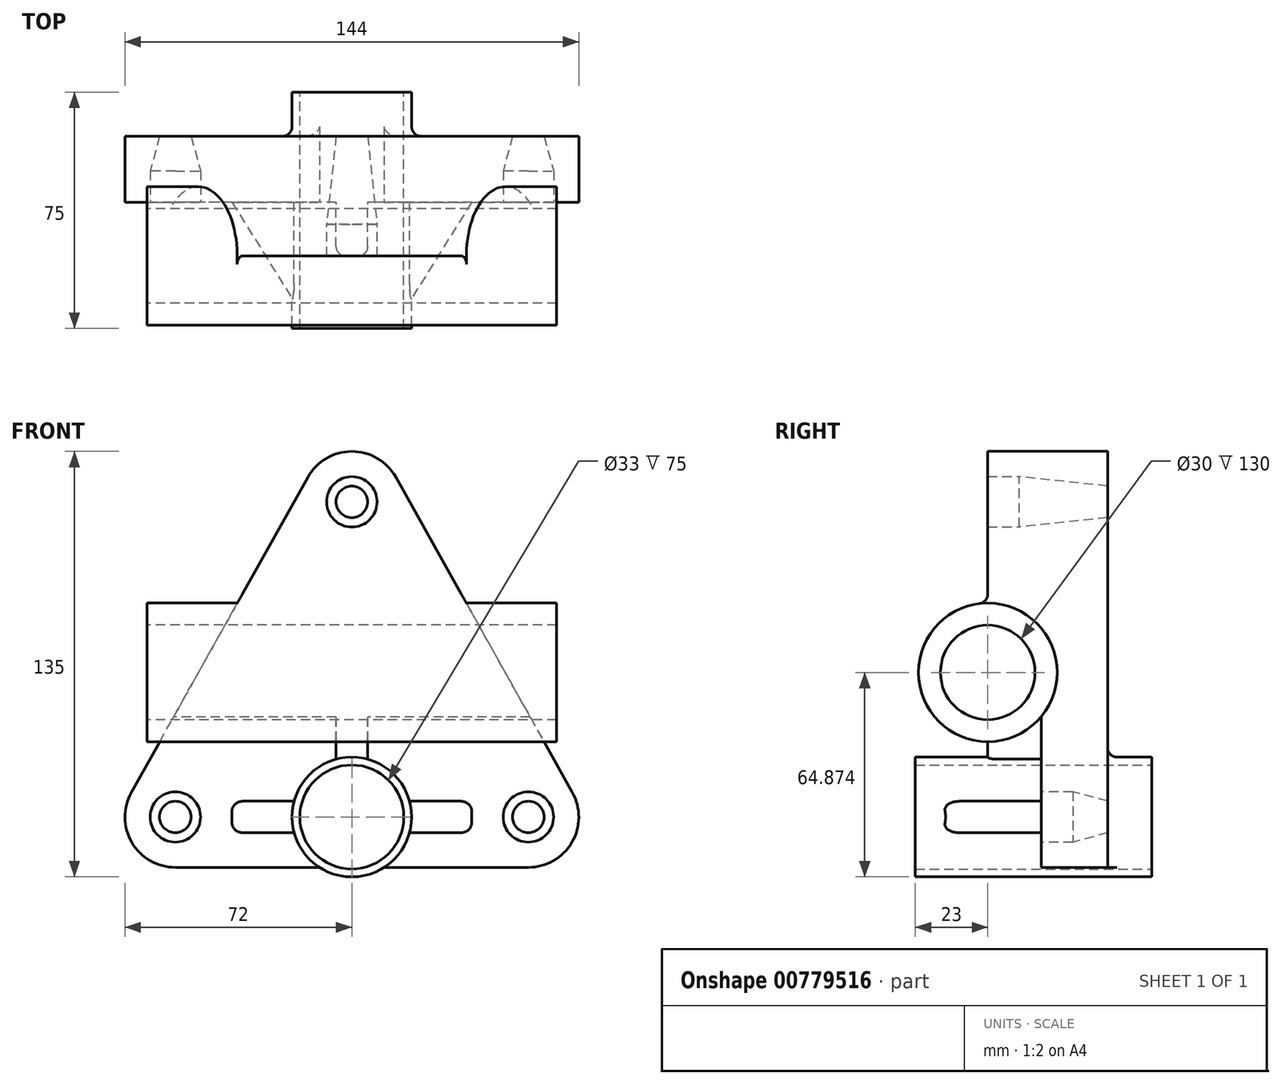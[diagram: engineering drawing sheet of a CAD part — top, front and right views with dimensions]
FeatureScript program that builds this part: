
annotation { "Feature Type Name" : "Feature", "Feature Type Description" : "" }
export const myFeature = defineFeature(function(context is Context, id is Id, definition is map)
    precondition{}
    {
        {
            var Q0;
            Q0=qCreatedBy(makeId("Front.planeOp"),FACE);
            var sketch = newSketch(context, id + "F0", { "sketchPlane" : qUnion([Q0])});
            skCircle(sketch, "E0", {"center": v(0, 0) * mm, "radius": 12.5 * mm});
            skCircle(sketch, "E1.0", {"center": v(0, 0) * mm, "radius": 19 * mm});
            skCircle(sketch, "E2.0", {"center": v(0, 0) * mm, "radius": 16.5 * mm});
            skCircle(sketch, "E3", {"center": v(-56, 0) * mm, "radius": 5 * mm});
            skCircle(sketch, "E4", {"center": v(-56, 0) * mm, "radius": 8 * mm});
            skCircle(sketch, "E5", {"center": v(56, 0) * mm, "radius": 8 * mm});
            skCircle(sketch, "E6", {"center": v(56, 0) * mm, "radius": 5 * mm});
            skCircle(sketch, "E7", {"center": v(0, 100) * mm, "radius": 5 * mm});
            skCircle(sketch, "E8", {"center": v(0, 100) * mm, "radius": 8 * mm});
            skArc(sketch, "E9.0", {"start": v(-69.96, 7.82) * mm, "mid": v(-69.8, -8.1) * mm, "end": v(-56, -16) * mm});
            skLineSegment(sketch, "E10", {"start": v(-10.25, -16) * mm, "end": v(-56, -16) * mm});
            skArc(sketch, "E11", {"start": v(13.96, 107.82) * mm, "mid": v(0, 116) * mm, "end": v(-13.96, 107.82) * mm});
            skLineSegment(sketch, "E12", {"start": v(-69.96, 7.82) * mm, "end": v(-13.96, 107.82) * mm});
            skLineSegment(sketch, "E13", {"start": v(10.25, -16) * mm, "end": v(56, -16) * mm});
            skArc(sketch, "E14.0", {"start": v(56, -16) * mm, "mid": v(69.8, -8.1) * mm, "end": v(69.96, 7.82) * mm});
            skLineSegment(sketch, "E15", {"start": v(13.96, 107.82) * mm, "end": v(69.96, 7.82) * mm});
            skLineSegment(sketch, "E16", {"start": v(0, 19) * mm, "end": v(0, -19) * mm, "construction": true});
            skLineSegment(sketch, "E17", {"start": v(-18.33, 5) * mm, "end": v(-38, 5) * mm});
            skLineSegment(sketch, "E18", {"start": v(-38, 5) * mm, "end": v(-38, -5) * mm});
            skLineSegment(sketch, "E19", {"start": v(-38, -5) * mm, "end": v(-18.33, -5) * mm});
            skLineSegment(sketch, "E20", {"start": v(18.33, 5) * mm, "end": v(38, 5) * mm});
            skLineSegment(sketch, "E21", {"start": v(38, 5) * mm, "end": v(38, -5) * mm});
            skLineSegment(sketch, "E22", {"start": v(38, -5) * mm, "end": v(18.33, -5) * mm});
            skLineSegment(sketch, "E23", {"start": v(-5, 31.73) * mm, "end": v(5, 31.73) * mm});
            skLineSegment(sketch, "E24", {"start": v(-5, 31.73) * mm, "end": v(-56.57, 31.73) * mm});
            skLineSegment(sketch, "E25", {"start": v(-56.57, 31.73) * mm, "end": v(56.57, 31.73) * mm});
            skLineSegment(sketch, "E26", {"start": v(-5, 31.73) * mm, "end": v(-5, 18.33) * mm});
            skLineSegment(sketch, "E27", {"start": v(5, 31.73) * mm, "end": v(5, 18.33) * mm});
            skSolve(sketch);
        }
        {
            var Q0;
            Q0=qCreatedBy(makeId("Right.planeOp"),FACE);
            var sketch = newSketch(context, id + "F1", { "sketchPlane" : qUnion([Q0])});
            skCircle(sketch, "E28", {"center": v(-17, 45.87) * mm, "radius": 22 * mm});
            skCircle(sketch, "E29", {"center": v(-17, 45.87) * mm, "radius": 15 * mm});
            skSolve(sketch);
        }
        {
            var Q0;
            Q0=makeQuery(id+"F0.imprint","IMPRINT",FACE,{"disambiguationData":[TD([[makeQuery(id+"F0.imprint","IMPRINT",EDGE,{"derivedFrom":sQuery(id+"F0.wireOp",EDGE,"E8")}),-1.0]])]});
            extrude(context, id + "F2", {"entities" : qUnion([Q0]), "depth" : 17 * mm, "offsetDistance" : 25 * mm});
        }
        {
            var Q0;
            Q0=makeQuery(id+"F0.imprint","IMPRINT",FACE,{"disambiguationData":[TD([[makeQuery(id+"F0.imprint","IMPRINT",EDGE,{"derivedFrom":sQuery(id+"F0.wireOp",EDGE,"E8")}),-1.0]])]});
            var Q1;
            Q1=makeQuery(id+"F0.imprint","IMPRINT",FACE,{"disambiguationData":[TD([[makeQuery(id+"F0.imprint","IMPRINT",EDGE,{"derivedFrom":sQuery(id+"F0.wireOp",EDGE,"E5")}),-1.0]])]});
            var Q2;
            Q2=makeQuery(id+"F0.imprint","IMPRINT",FACE,{"disambiguationData":[TD([[makeQuery(id+"F0.imprint","IMPRINT",EDGE,{"derivedFrom":sQuery(id+"F0.wireOp",EDGE,"E4")}),-1.0]])]});
            var Q3;
            {var subQ0=sQuery(id+"F0.wireOp",EDGE,"E20");Q3=makeQuery(id+"F0.imprint","IMPRINT",FACE,{"disambiguationData":[TD([[makeQuery(id+"F0.imprint","IMPRINT",EDGE,{"derivedFrom":subQ0}),-1.0]])]});}
            var Q4;
            {var subQ0=sQuery(id+"F0.wireOp",EDGE,"E17");Q4=makeQuery(id+"F0.imprint","IMPRINT",FACE,{"disambiguationData":[TD([[makeQuery(id+"F0.imprint","IMPRINT",EDGE,{"derivedFrom":subQ0}),1.0]])]});}
            extrude(context, id + "F3", {"entities" : qUnion([Q0, Q1, Q2, Q3, Q4]), "operationType" : NewBodyOperationType.ADD, "oppositeDirection" : true, "depth" : 21 * mm, "offsetDistance" : 25 * mm});
        }
        {
            var Q0;
            Q0=makeQuery(id+"F1.imprint","IMPRINT",FACE,{"disambiguationData":[TD([[makeQuery(id+"F1.imprint","IMPRINT",EDGE,{"derivedFrom":sQuery(id+"F1.wireOp",EDGE,"E28")}),1.0]])]});
            extrude(context, id + "F4", {"entities" : qUnion([Q0]), "operationType" : NewBodyOperationType.ADD, "endBound" : BoundingType.SYMMETRIC, "depth" : 130 * mm, "offsetDistance" : 25 * mm});
        }
        {
            var Q0;
            Q0=makeQuery(id+"F1.imprint","IMPRINT",FACE,{"disambiguationData":[TD([[makeQuery(id+"F1.imprint","IMPRINT",EDGE,{"derivedFrom":sQuery(id+"F1.wireOp",EDGE,"E29")}),1.0]])]});
            extrude(context, id + "F5", {"entities" : qUnion([Q0]), "operationType" : NewBodyOperationType.REMOVE, "endBound" : BoundingType.SYMMETRIC, "oppositeDirection" : true, "depth" : 130 * mm, "offsetDistance" : 25 * mm});
        }
        {
            var Q0;
            {var subQ0=sQuery(id+"F0.wireOp",EDGE,"E17");Q0=makeQuery(id+"F0.imprint","IMPRINT",FACE,{"disambiguationData":[TD([[makeQuery(id+"F0.imprint","IMPRINT",EDGE,{"derivedFrom":subQ0}),1.0]])]});}
            var Q1;
            {var subQ0=sQuery(id+"F0.wireOp",EDGE,"E20");Q1=makeQuery(id+"F0.imprint","IMPRINT",FACE,{"disambiguationData":[TD([[makeQuery(id+"F0.imprint","IMPRINT",EDGE,{"derivedFrom":subQ0}),-1.0]])]});}
            extrude(context, id + "F6", {"entities" : qUnion([Q0, Q1]), "operationType" : NewBodyOperationType.ADD, "depth" : 32 * mm, "offsetDistance" : 25 * mm});
        }
        {
            var Q0;
            Q0=makeQuery(id+"F0.imprint","IMPRINT",FACE,{"disambiguationData":[TD([[makeQuery(id+"F0.imprint","IMPRINT",EDGE,{"derivedFrom":sQuery(id+"F0.wireOp",EDGE,"E2.0")}),-1.0]])]});
            extrude(context, id + "F7", {"entities" : qUnion([Q0]), "depth" : 40 * mm, "offsetDistance" : 25 * mm});
        }
        {
            var Q0;
            Q0=makeQuery(id+"F0.imprint","IMPRINT",FACE,{"disambiguationData":[TD([[makeQuery(id+"F0.imprint","IMPRINT",EDGE,{"derivedFrom":sQuery(id+"F0.wireOp",EDGE,"E2.0")}),-1.0]])]});
            extrude(context, id + "F8", {"entities" : qUnion([Q0]), "oppositeDirection" : true, "depth" : 35 * mm, "offsetDistance" : 25 * mm});
        }
        {
            var Q0;
            Q0=makeQuery(id+"F6.opExtrude","CAP_EDGE",EDGE,{"disambiguationData":[OSD([sQuery(id+"F0.wireOp",EDGE,"E18")])],"isStart":false});
            chamfer(context, id + "F9", {"entities" : qUnion([Q0]), "chamferType" : ChamferType.TWO_OFFSETS, "width1" : 20 * mm, "oppositeDirection" : false, "width2" : 32 * mm, "tangentPropagation" : true});
        }
        {
            var Q0;
            Q0=makeQuery(id+"F6.opExtrude","CAP_EDGE",EDGE,{"disambiguationData":[OSD([sQuery(id+"F0.wireOp",EDGE,"E21")])],"isStart":false});
            chamfer(context, id + "F10", {"entities" : qUnion([Q0]), "chamferType" : ChamferType.TWO_OFFSETS, "width1" : 32 * mm, "oppositeDirection" : false, "width2" : 20 * mm, "tangentPropagation" : true});
        }
        {
            var Q0;
            {var subQ0=sQuery(id+"F0.wireOp",EDGE,"E26");Q0=makeQuery(id+"F0.imprint","IMPRINT",FACE,{"disambiguationData":[TD([[makeQuery(id+"F0.imprint","IMPRINT",EDGE,{"derivedFrom":subQ0}),1.0]])]});}
            extrude(context, id + "F11", {"entities" : qUnion([Q0]), "operationType" : NewBodyOperationType.ADD, "oppositeDirection" : true, "depth" : 21 * mm, "offsetDistance" : 25 * mm});
        }
        {
            var Q0;
            {var subQ0=sQuery(id+"F0.wireOp",EDGE,"E26");Q0=makeQuery(id+"F0.imprint","IMPRINT",FACE,{"disambiguationData":[TD([[makeQuery(id+"F0.imprint","IMPRINT",EDGE,{"derivedFrom":subQ0}),1.0]])]});}
            extrude(context, id + "F12", {"entities" : qUnion([Q0]), "operationType" : NewBodyOperationType.ADD, "depth" : 17 * mm, "offsetDistance" : 25 * mm});
        }
        {
            var Q0;
            Q0=makeQuery(id+"F1.imprint","IMPRINT",FACE,{"disambiguationData":[TD([[makeQuery(id+"F1.imprint","IMPRINT",EDGE,{"derivedFrom":sQuery(id+"F1.wireOp",EDGE,"E29")}),1.0]])]});
            extrude(context, id + "F13", {"entities" : qUnion([Q0]), "operationType" : NewBodyOperationType.REMOVE, "endBound" : BoundingType.SYMMETRIC, "oppositeDirection" : true, "depth" : 130 * mm, "offsetDistance" : 25 * mm});
        }
        {
            var Q0;
            {var subQ0=sQuery(id+"F0.wireOp",EDGE,"E27");var subQ1=sQuery(id+"F0.wireOp",EDGE,"E26");var subQ2=sQuery(id+"F0.wireOp",EDGE,"E25");var subQ3=sQuery(id+"F0.wireOp",EDGE,"E1.0");Q0=makeQuery(id+"F11.boolean.opBoolean","MERGE",FACE,{"derivedFrom":[makeQuery(id+"F3.opExtrude","CAP_FACE",FACE,{"disambiguationData":[OSD([subQ3,sQuery(id+"F0.wireOp",EDGE,"E4"),sQuery(id+"F0.wireOp",EDGE,"E5"),sQuery(id+"F0.wireOp",EDGE,"E8"),sQuery(id+"F0.wireOp",EDGE,"E9.0"),sQuery(id+"F0.wireOp",EDGE,"E10"),sQuery(id+"F0.wireOp",EDGE,"E11"),sQuery(id+"F0.wireOp",EDGE,"E12"),sQuery(id+"F0.wireOp",EDGE,"E13"),sQuery(id+"F0.wireOp",EDGE,"E14.0"),sQuery(id+"F0.wireOp",EDGE,"E15"),subQ2,subQ1,subQ0])],"isStart":false}),makeQuery(id+"F11.opExtrude","CAP_FACE",FACE,{"disambiguationData":[OSD([subQ3,subQ2,subQ1,subQ0])],"isStart":false})]});}
            var sketch = newSketch(context, id + "F14", { "sketchPlane" : qUnion([Q0])});
            skCircle(sketch, "E30", {"center": v(-56, 0) * mm, "radius": 8 * mm});
            skCircle(sketch, "E31", {"center": v(56, 0) * mm, "radius": 8 * mm});
            skCircle(sketch, "E32", {"center": v(0, 100) * mm, "radius": 8 * mm});
            skCircle(sketch, "E33", {"center": v(0, 100) * mm, "radius": 5 * mm});
            skCircle(sketch, "E34", {"center": v(-56, 0) * mm, "radius": 5 * mm});
            skCircle(sketch, "E35", {"center": v(56, 0) * mm, "radius": 5 * mm});
            skSolve(sketch);
        }
        {
            var Q0;
            Q0=makeQuery(id+"F14.imprint","IMPRINT",FACE,{"disambiguationData":[TD([[makeQuery(id+"F14.imprint","IMPRINT",EDGE,{"derivedFrom":sQuery(id+"F14.wireOp",EDGE,"E30")}),-1.0]])]});
            var Q1;
            Q1=makeQuery(id+"F14.imprint","IMPRINT",FACE,{"disambiguationData":[TD([[makeQuery(id+"F14.imprint","IMPRINT",EDGE,{"derivedFrom":sQuery(id+"F14.wireOp",EDGE,"E31")}),-1.0]])]});
            extrude(context, id + "F15", {"entities" : qUnion([Q0, Q1]), "operationType" : NewBodyOperationType.ADD, "oppositeDirection" : true, "depth" : 11 * mm, "offsetDistance" : 25 * mm});
        }
        {
            var Q0;
            Q0=makeQuery(id+"F14.imprint","IMPRINT",FACE,{"disambiguationData":[TD([[makeQuery(id+"F14.imprint","IMPRINT",EDGE,{"derivedFrom":sQuery(id+"F14.wireOp",EDGE,"E32")}),-1.0]])]});
            extrude(context, id + "F16", {"entities" : qUnion([Q0]), "operationType" : NewBodyOperationType.ADD, "oppositeDirection" : true, "depth" : 28 * mm, "offsetDistance" : 25 * mm});
        }
        {
            var Q0;
            Q0=makeQuery(id+"F15.opExtrude","CAP_EDGE",EDGE,{"disambiguationData":[OSD([sQuery(id+"F14.wireOp",EDGE,"E35")])],"isStart":false});
            chamfer(context, id + "F17", {"entities" : qUnion([Q0]), "chamferType" : ChamferType.TWO_OFFSETS, "width1" : 3 * mm, "oppositeDirection" : false, "width2" : 11 * mm, "tangentPropagation" : true});
        }
        {
            var Q0;
            Q0=makeQuery(id+"F15.opExtrude","CAP_EDGE",EDGE,{"disambiguationData":[OSD([sQuery(id+"F14.wireOp",EDGE,"E34")])],"isStart":false});
            chamfer(context, id + "F18", {"entities" : qUnion([Q0]), "chamferType" : ChamferType.TWO_OFFSETS, "width1" : 3 * mm, "oppositeDirection" : false, "width2" : 11 * mm, "tangentPropagation" : true});
        }
        {
            var Q0;
            Q0=makeQuery(id+"F16.opExtrude","CAP_EDGE",EDGE,{"disambiguationData":[OSD([sQuery(id+"F14.wireOp",EDGE,"E33")])],"isStart":false});
            chamfer(context, id + "F19", {"entities" : qUnion([Q0]), "chamferType" : ChamferType.TWO_OFFSETS, "width1" : 3 * mm, "oppositeDirection" : false, "width2" : 28 * mm, "tangentPropagation" : true});
        }
        {
            var Q0;
            Q0=makeQuery(id+"F10.opChamfer","BLEND_EDGE",EDGE,{"blendedFrom":[makeQuery(id+"F6.opExtrude","CAP_EDGE",EDGE,{"disambiguationData":[OSD([sQuery(id+"F0.wireOp",EDGE,"E21")])],"isStart":false}),makeQuery(id+"F6.opExtrude","SWEPT_FACE",FACE,{"disambiguationData":[OSD([sQuery(id+"F0.wireOp",EDGE,"E20")])]})],"blendedInto":[makeQuery(id+"F6.opExtrude","SWEPT_FACE",FACE,{"disambiguationData":[OSD([sQuery(id+"F0.wireOp",EDGE,"E20")])]})]});
            var Q1;
            Q1=makeQuery(id+"F10.opChamfer","BLEND_EDGE",EDGE,{"blendedFrom":[makeQuery(id+"F6.opExtrude","CAP_EDGE",EDGE,{"disambiguationData":[OSD([sQuery(id+"F0.wireOp",EDGE,"E21")])],"isStart":false}),makeQuery(id+"F6.opExtrude","SWEPT_FACE",FACE,{"disambiguationData":[OSD([sQuery(id+"F0.wireOp",EDGE,"E22")])]})],"blendedInto":[makeQuery(id+"F6.opExtrude","SWEPT_FACE",FACE,{"disambiguationData":[OSD([sQuery(id+"F0.wireOp",EDGE,"E22")])]})]});
            var Q2;
            Q2=makeQuery(id+"F9.opChamfer","BLEND_EDGE",EDGE,{"blendedFrom":[makeQuery(id+"F6.opExtrude","CAP_EDGE",EDGE,{"disambiguationData":[OSD([sQuery(id+"F0.wireOp",EDGE,"E18")])],"isStart":false}),makeQuery(id+"F6.opExtrude","SWEPT_FACE",FACE,{"disambiguationData":[OSD([sQuery(id+"F0.wireOp",EDGE,"E19")])]})],"blendedInto":[makeQuery(id+"F6.opExtrude","SWEPT_FACE",FACE,{"disambiguationData":[OSD([sQuery(id+"F0.wireOp",EDGE,"E19")])]})]});
            var Q3;
            Q3=makeQuery(id+"F9.opChamfer","BLEND_EDGE",EDGE,{"blendedFrom":[makeQuery(id+"F6.opExtrude","CAP_EDGE",EDGE,{"disambiguationData":[OSD([sQuery(id+"F0.wireOp",EDGE,"E18")])],"isStart":false}),makeQuery(id+"F6.opExtrude","SWEPT_FACE",FACE,{"disambiguationData":[OSD([sQuery(id+"F0.wireOp",EDGE,"E17")])]})],"blendedInto":[makeQuery(id+"F6.opExtrude","SWEPT_FACE",FACE,{"disambiguationData":[OSD([sQuery(id+"F0.wireOp",EDGE,"E17")])]})]});
            var Q4;
            {var subQ0=sQuery(id+"F0.wireOp",EDGE,"E26");Q4=makeQuery(id+"F12.boolean.opBoolean","SPLIT",EDGE,{"disambiguationData":[TD([makeQuery(id+"F4.opExtrude","SWEPT_FACE",FACE,{"disambiguationData":[OSD([sQuery(id+"F1.wireOp",EDGE,"E28")])]})])],"derivedFrom":makeQuery(id+"F12.opExtrude","CAP_EDGE",EDGE,{"disambiguationData":[OSD([subQ0])],"isStart":false})});}
            var Q5;
            {var subQ0=sQuery(id+"F0.wireOp",EDGE,"E27");Q5=makeQuery(id+"F12.boolean.opBoolean","SPLIT",EDGE,{"disambiguationData":[TD([makeQuery(id+"F4.opExtrude","SWEPT_FACE",FACE,{"disambiguationData":[OSD([sQuery(id+"F1.wireOp",EDGE,"E28")])]})])],"derivedFrom":makeQuery(id+"F12.opExtrude","CAP_EDGE",EDGE,{"disambiguationData":[OSD([subQ0])],"isStart":false})});}
            var Q6;
            Q6=makeQuery(id+"F4.boolean.opBoolean","INTERSECT",EDGE,{"derivedFrom":[makeQuery(id+"F2.opExtrude","CAP_FACE",FACE,{"disambiguationData":[OSD([sQuery(id+"F0.wireOp",EDGE,"E8"),sQuery(id+"F0.wireOp",EDGE,"E11"),sQuery(id+"F0.wireOp",EDGE,"E12"),sQuery(id+"F0.wireOp",EDGE,"E15"),sQuery(id+"F0.wireOp",EDGE,"E25")])],"isStart":false}),makeQuery(id+"F4.opExtrude","SWEPT_FACE",FACE,{"disambiguationData":[OSD([sQuery(id+"F1.wireOp",EDGE,"E28")])]})]});
            var Q7;
            {var subQ0=sQuery(id+"F0.wireOp",EDGE,"E25");var subQ1=makeQuery(id+"F3.opExtrude","SWEPT_FACE",FACE,{"disambiguationData":[OSD([subQ0])]});var subQ2=sQuery(id+"F0.wireOp",EDGE,"E12");var subQ3=makeQuery(id+"F2.opExtrude","SWEPT_FACE",FACE,{"disambiguationData":[OSD([subQ0])]});var subQ4=makeQuery(id+"F4.opExtrude","SWEPT_FACE",FACE,{"disambiguationData":[OSD([sQuery(id+"F1.wireOp",EDGE,"E28")])]});Q7=makeQuery(id+"F12.boolean.opBoolean","SPLIT",EDGE,{"disambiguationData":[TD([makeQuery(id+"F2.opExtrude","SWEPT_FACE",FACE,{"disambiguationData":[OSD([subQ2])]})])],"derivedFrom":makeQuery(id+"F4.boolean.opBoolean","INTERSECT",EDGE,{"derivedFrom":[makeQuery(id+"F3.boolean.opBoolean","MERGE",FACE,{"derivedFrom":[subQ3,subQ1]}),subQ4]})});}
            var Q8;
            {var subQ0=sQuery(id+"F0.wireOp",EDGE,"E15");var subQ1=sQuery(id+"F0.wireOp",EDGE,"E25");var subQ2=makeQuery(id+"F2.opExtrude","SWEPT_FACE",FACE,{"disambiguationData":[OSD([subQ1])]});var subQ3=makeQuery(id+"F3.opExtrude","SWEPT_FACE",FACE,{"disambiguationData":[OSD([subQ1])]});var subQ4=makeQuery(id+"F4.opExtrude","SWEPT_FACE",FACE,{"disambiguationData":[OSD([sQuery(id+"F1.wireOp",EDGE,"E28")])]});Q8=makeQuery(id+"F12.boolean.opBoolean","SPLIT",EDGE,{"disambiguationData":[TD([makeQuery(id+"F2.opExtrude","SWEPT_FACE",FACE,{"disambiguationData":[OSD([subQ0])]})])],"derivedFrom":makeQuery(id+"F4.boolean.opBoolean","INTERSECT",EDGE,{"derivedFrom":[makeQuery(id+"F3.boolean.opBoolean","MERGE",FACE,{"derivedFrom":[subQ2,subQ3]}),subQ4]})});}
            var Q9;
            Q9=makeQuery(id+"F12.opExtrude","CAP_EDGE",EDGE,{"disambiguationData":[OSD([sQuery(id+"F0.wireOp",EDGE,"E1.0")])],"isStart":false});
            var Q10;
            {var subQ0=sQuery(id+"F0.wireOp",EDGE,"E1.0");var subQ2=makeQuery(id+"F0.imprint","INTERSECT",VERTEX,{"derivedFrom":[subQ0,sQuery(id+"F0.wireOp",EDGE,"E17")]});var subQ3=makeQuery(id+"F0.imprint","INTERSECT",VERTEX,{"derivedFrom":[subQ0,sQuery(id+"F0.wireOp",EDGE,"E20")]});Q10=makeQuery(id+"F11.boolean.opBoolean","MERGE",EDGE,{"derivedFrom":[makeQuery(id+"F3.opExtrude","CAP_EDGE",EDGE,{"disambiguationData":[OSD([subQ0]),TDD([makeQuery(id+"F0.imprint","IMPRINT",EDGE,{"disambiguationData":[TD([[subQ3,-1.0]])],"derivedFrom":subQ0}),makeQuery(id+"F0.imprint","IMPRINT",EDGE,{"disambiguationData":[TD([[makeQuery(id+"F0.imprint","INTERSECT",VERTEX,{"derivedFrom":[subQ0,sQuery(id+"F0.wireOp",EDGE,"E13")]}),-1.0]])],"derivedFrom":subQ0}),makeQuery(id+"F0.imprint","IMPRINT",EDGE,{"disambiguationData":[TD([[subQ3,1.0]])],"derivedFrom":subQ0})])],"isStart":false}),makeQuery(id+"F3.opExtrude","CAP_EDGE",EDGE,{"disambiguationData":[OSD([subQ0]),TDD([makeQuery(id+"F0.imprint","IMPRINT",EDGE,{"disambiguationData":[TD([[subQ2,1.0]])],"derivedFrom":subQ0}),makeQuery(id+"F0.imprint","IMPRINT",EDGE,{"disambiguationData":[TD([[subQ2,-1.0]])],"derivedFrom":subQ0}),makeQuery(id+"F0.imprint","IMPRINT",EDGE,{"disambiguationData":[TD([[makeQuery(id+"F0.imprint","INTERSECT",VERTEX,{"derivedFrom":[subQ0,sQuery(id+"F0.wireOp",EDGE,"E10")]}),1.0]])],"derivedFrom":subQ0})])],"isStart":false}),makeQuery(id+"F11.opExtrude","CAP_EDGE",EDGE,{"disambiguationData":[OSD([subQ0])],"isStart":false})]});}
            fillet(context, id + "F20", {"entities" : qUnion([Q0, Q1, Q2, Q3, Q4, Q5, Q6, Q7, Q8, Q9, Q10]), "radius" : 3 * mm, "tangentPropagation" : true, "allowEdgeOverflow" : false});
        }
    });
